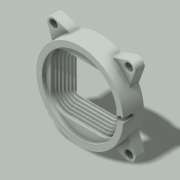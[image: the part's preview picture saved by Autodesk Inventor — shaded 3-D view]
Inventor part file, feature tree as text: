
AUTODESK INVENTOR PART (.ipt)
format: ipt  version: 2015 (Build 190159000, 159)  size: 616,960 bytes
history: native  units: in
note: dims shown in document units (in); Inventor stores cm internally (conversion verified against a paired STEP export)
features: extrude x17, sketch x17, reference x4, fillet x1
ambient origin geometry x8: Origin, YZ Plane, XZ Plane, XY Plane, X Axis, Y Axis, Z Axis, Center Point
bodies: Solid1 (feature_tree)
feature tree (39):
  extrude  "Extrusion1"  Depth=0.3937in TaperAngle=0.0deg
  extrude  "Extrusion14"  Depth=0.315in TaperAngle=0.0deg
  extrude  "Extrusion15"  Depth=0.6339in
  extrude  "Extrusion39"  Depth=0.0394in
  extrude  "Extrusion17"  Depth=0.315in TaperAngle=0.0deg
  extrude  "Extrusion18"  Depth=0.2756in TaperAngle=0.0deg
  extrude  "Extrusion19"  Depth=0.2362in TaperAngle=0.0deg
  extrude  "Extrusion20"  Depth=0.1969in TaperAngle=0.0deg
  extrude  "Extrusion21"  Depth=0.1575in TaperAngle=0.0deg
  extrude  "Extrusion22"  Depth=0.1181in TaperAngle=0.0deg
  extrude  "Extrusion23"  Depth=0.0787in TaperAngle=0.0deg
  extrude  "Extrusion24"  Depth=0.0394in TaperAngle=0.0deg
  extrude  "Extrusion25"  Depth=0.9843in
  extrude  "Extrusion38"  Depth=0.1102in
  sketch  "Sketch40"  dims[d137=0.0394in d138=0.0394in d139=0.0in]
  extrude  "Extrusion40"  Depth=2.3622in
  extrude  "Extrusion41"  Depth=0.0197in
  extrude  "Extrusion42"  Depth=0.0197in
  fillet  "Fillet1"  Radius=0.1575in
  sketch  "Sketch1"  dims[d9=0.1969in d10=0.0in]
  reference  "Reference2"
  reference  "Reference3"
  reference  "Reference4"
  reference  "Reference5"
  sketch  "Sketch15"  dims[d11=0.1181in d12=0.1181in d35=0.3937in d36=0.5906in d37=0.7874in d38=0.9843in d39=0.3937in d40=0.5906in d41=1.1811in d42=1.378in d43=1.5748in d44=1.7717in d94=0.1969in d95=0.0in]
  sketch  "Sketch17"  dims[d96=1.811in d100=0.315in d101=0.0in]
  sketch  "Sketch18"  dims[d111=0.8189in d112=0.6339in]
  sketch  "Sketch19"  dims[d113=0.3543in d114=0.0in d115=0.0394in]
  sketch  "Sketch20"  dims[d116=0.0394in d117=0.315in d118=0.0in]
  sketch  "Sketch21"  dims[d119=0.0394in d120=0.2756in d121=0.0in]
  sketch  "Sketch22"  dims[d122=0.0394in d123=0.2362in d124=0.0in]
  sketch  "Sketch23"  dims[d125=0.0394in d126=0.1969in d127=0.0in]
  sketch  "Sketch24"  dims[d128=0.0394in d129=0.1575in d130=0.0in]
  sketch  "Sketch25"  dims[d131=0.0394in d132=0.1181in d133=0.0in]
  sketch  "Sketch39"  dims[d134=0.0394in d135=0.0787in d136=0.0in]
  sketch  "Sketch41"  dims[d217=0.9843in d219=0.9843in]
  sketch  "Sketch42"  dims[d220=0.063in d221=0.0in d222=0.1102in]
  sketch  "Sketch43"  dims[d223=0.2756in d231=2.3622in]
  sketch  "Sketch44"  dims[d233=1.5748in d234=1.1002in d264=2.2in d287=0.1575in d288=0.0787in d289=0.0in d291=1.5748in d292=1.5748in d293=0.1102in d294=0.1102in d295=1.0651in d296=1.0651in d297=2.2441in d298=1.2179in d299=0.9075in d300=1.0651in d301=0.1378in d302=1.0651in d303=0.9075in d304=0.1575in d305=0.1575in d306=1.5748in d307=1.815in d308=1.811in d310=1.9055in d311=0.0787in d312=0.0in d313=0.2992in d314=0.0in d315=0.1181in d317=0.8484in d318=0.1181in d319=0.0866in d320=0.1181in d321=0.0512in d323=0.1181in d324=0.0in d325=0.0197in]
